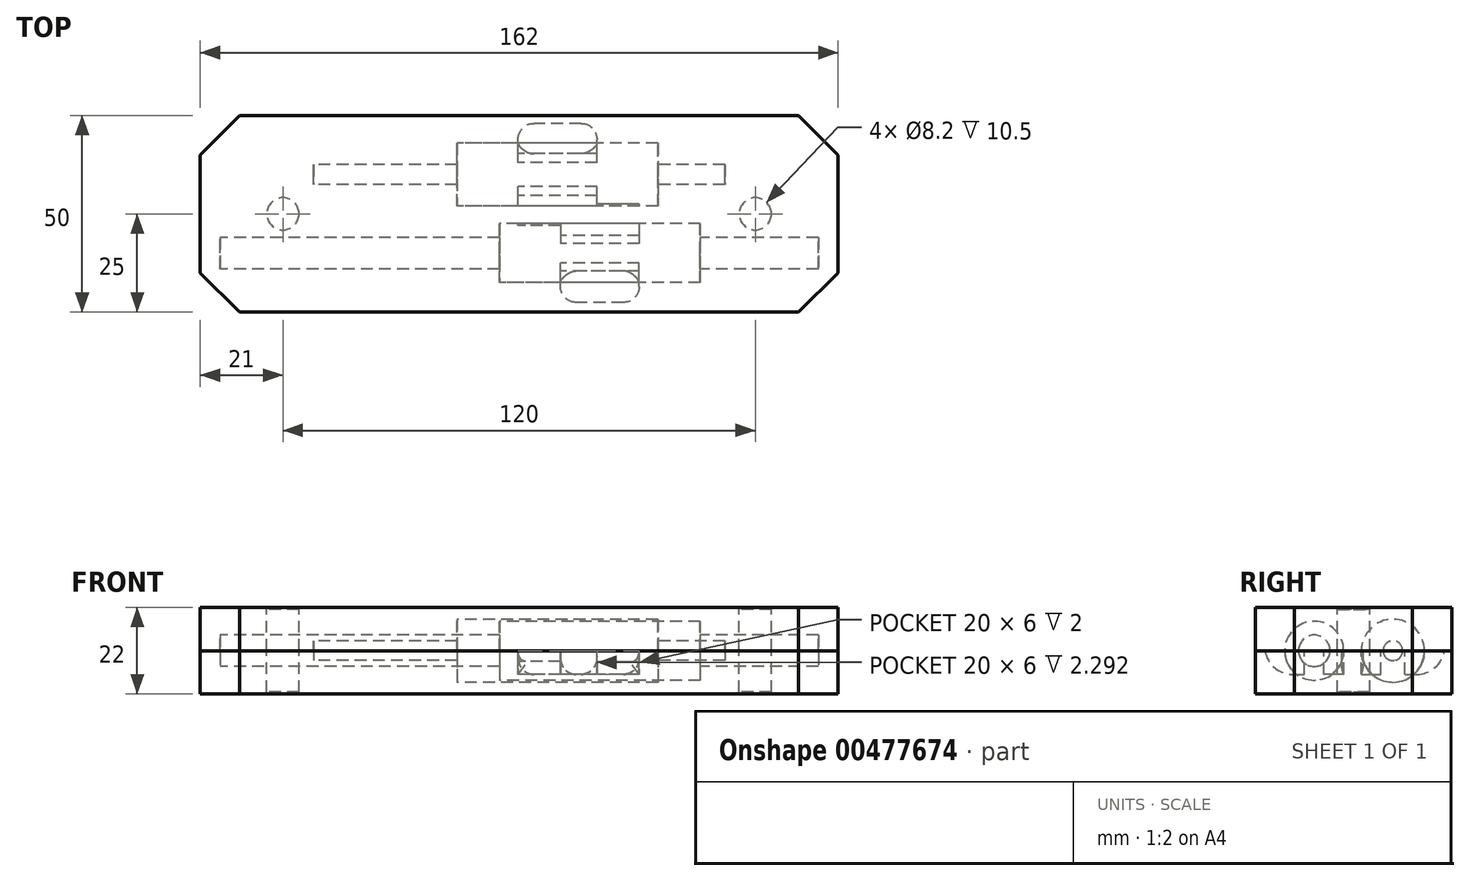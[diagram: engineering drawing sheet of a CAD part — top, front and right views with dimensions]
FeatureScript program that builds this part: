
annotation { "Feature Type Name" : "Feature", "Feature Type Description" : "" }
export const myFeature = defineFeature(function(context is Context, id is Id, definition is map)
    precondition{}
    {
        {
            var Q0;
            Q0=qCreatedBy(makeId("Top.planeOp"),FACE);
            var sketch = newSketch(context, id + "F0", { "sketchPlane" : qUnion([Q0])});
            skLineSegment(sketch, "E0", {"start": v(-52.25, 10) * mm, "end": v(52.25, 10) * mm});
            skLineSegment(sketch, "E1", {"start": v(52.25, 10) * mm, "end": v(52.25, 12.5) * mm});
            skLineSegment(sketch, "E2", {"start": v(52.25, 12.5) * mm, "end": v(35.25, 12.5) * mm});
            skLineSegment(sketch, "E3", {"start": v(35.25, 12.5) * mm, "end": v(35.25, 18) * mm});
            skLineSegment(sketch, "E4", {"start": v(35.25, 18) * mm, "end": v(-15.75, 18) * mm});
            skLineSegment(sketch, "E5", {"start": v(-15.75, 18) * mm, "end": v(-15.75, 12.5) * mm});
            skLineSegment(sketch, "E6", {"start": v(-15.75, 12.5) * mm, "end": v(-52.25, 12.5) * mm});
            skLineSegment(sketch, "E7", {"start": v(-52.25, 12.5) * mm, "end": v(-52.25, 10) * mm});
            skLineSegment(sketch, "E8", {"start": v(-76, -10) * mm, "end": v(76, -10) * mm});
            skLineSegment(sketch, "E9", {"start": v(76, -10) * mm, "end": v(76, -14) * mm});
            skLineSegment(sketch, "E10", {"start": v(76, -14) * mm, "end": v(46, -14) * mm});
            skLineSegment(sketch, "E11", {"start": v(46, -14) * mm, "end": v(46, -17.5) * mm});
            skLineSegment(sketch, "E12", {"start": v(46, -17.5) * mm, "end": v(-5, -17.5) * mm});
            skLineSegment(sketch, "E13", {"start": v(-5, -17.5) * mm, "end": v(-5, -14) * mm});
            skLineSegment(sketch, "E14", {"start": v(-5, -14) * mm, "end": v(-76, -14) * mm});
            skLineSegment(sketch, "E15", {"start": v(-76, -14) * mm, "end": v(-76, -10) * mm});
            skLineSegment(sketch, "E16", {"start": v(0, -10) * mm, "end": v(0, 0) * mm, "construction": true});
            skLineSegment(sketch, "E17", {"start": v(0, 10) * mm, "end": v(0, 0) * mm, "construction": true});
            skSolve(sketch);
        }
        {
            var Q0;
            Q0=makeQuery(id+"F0.imprint","IMPRINT",FACE,{"disambiguationData":[TD([[makeQuery(id+"F0.imprint","IMPRINT",EDGE,{"derivedFrom":sQuery(id+"F0.wireOp",EDGE,"E0")}),1.0]])]});
            var Q1;
            Q1=sQuery(id+"F0.wireOp",EDGE,"E0");
            revolve(context, id + "F1", {"entities" : qUnion([Q0]), "axis" : qUnion([Q1]), "revolveType" : RevolveType.FULL});
        }
        {
            var Q0;
            Q0=makeQuery(id+"F0.imprint","IMPRINT",FACE,{"disambiguationData":[TD([[makeQuery(id+"F0.imprint","IMPRINT",EDGE,{"derivedFrom":sQuery(id+"F0.wireOp",EDGE,"E8")}),-1.0]])]});
            var Q1;
            Q1=sQuery(id+"F0.wireOp",EDGE,"E8");
            revolve(context, id + "F2", {"entities" : qUnion([Q0]), "axis" : qUnion([Q1]), "revolveType" : RevolveType.FULL});
        }
        {
            var Q0;
            Q0=qCreatedBy(makeId("Top.planeOp"),FACE);
            var sketch = newSketch(context, id + "F3", { "sketchPlane" : qUnion([Q0])});
            skLineSegment(sketch, "E18.bottom", {"start": v(81, -25) * mm, "end": v(-81, -25) * mm});
            skLineSegment(sketch, "E18.top", {"start": v(81, 25) * mm, "end": v(-81, 25) * mm});
            skLineSegment(sketch, "E18.left", {"start": v(81, -25) * mm, "end": v(81, 25) * mm});
            skLineSegment(sketch, "E18.right", {"start": v(-81, -25) * mm, "end": v(-81, 25) * mm});
            skPoint(sketch, "E18.middle", {"position": v(0, 0) * mm});
            skSolve(sketch);
        }
        {
            var Q0;
            Q0=makeQuery(id+"F3.imprint","IMPRINT",FACE,{"disambiguationData":[TD([[makeQuery(id+"F3.imprint","IMPRINT",EDGE,{"derivedFrom":sQuery(id+"F3.wireOp",EDGE,"E18.bottom")}),-1.0]])]});
            extrude(context, id + "F4", {"entities" : qUnion([Q0]), "oppositeDirection" : true, "depth" : 11 * mm});
        }
        {
            var Q0;
            Q0=makeQuery(id+"F4.opExtrude","CAP_FACE",FACE,{"disambiguationData":[OSD([sQuery(id+"F3.wireOp",EDGE,"E18.bottom"),sQuery(id+"F3.wireOp",EDGE,"E18.top"),sQuery(id+"F3.wireOp",EDGE,"E18.left"),sQuery(id+"F3.wireOp",EDGE,"E18.right")])],"isStart":true});
            var sketch = newSketch(context, id + "F5", { "sketchPlane" : qUnion([Q0])});
            skLineSegment(sketch, "E19.bottom", {"start": v(81, -25) * mm, "end": v(-81, -25) * mm});
            skLineSegment(sketch, "E19.top", {"start": v(81, 25) * mm, "end": v(-81, 25) * mm});
            skLineSegment(sketch, "E19.left", {"start": v(81, -25) * mm, "end": v(81, 25) * mm});
            skLineSegment(sketch, "E19.right", {"start": v(-81, -25) * mm, "end": v(-81, 25) * mm});
            skPoint(sketch, "E19.middle", {"position": v(0, 0) * mm});
            skSolve(sketch);
        }
        {
            var Q0;
            Q0=makeQuery(id+"F5.imprint","IMPRINT",FACE,{"disambiguationData":[TD([[makeQuery(id+"F5.imprint","IMPRINT",EDGE,{"derivedFrom":sQuery(id+"F5.wireOp",EDGE,"E19.bottom")}),-1.0]])]});
            var Q1;
            Q1=makeQuery(id+"F5.imprint","IMPRINT",FACE,{"disambiguationData":[TD([[makeQuery(id+"F5.imprint","IMPRINT",EDGE,{"derivedFrom":makeQuery(id+"F4.opExtrude","CAP_EDGE",EDGE,{"disambiguationData":[OSD([sQuery(id+"F3.wireOp",EDGE,"E18.bottom")])],"isStart":true})}),-1.0]])]});
            extrude(context, id + "F6", {"entities" : qUnion([Q0, Q1]), "depth" : 11 * mm});
        }
        {
            var Q0;
            Q0=makeQuery(id+"F6.opExtrude","CAP_FACE",FACE,{"disambiguationData":[OSD([sQuery(id+"F5.wireOp",EDGE,"E19.bottom"),sQuery(id+"F5.wireOp",EDGE,"E19.top"),sQuery(id+"F5.wireOp",EDGE,"E19.left"),sQuery(id+"F5.wireOp",EDGE,"E19.right")])],"isStart":true});
            var sketch = newSketch(context, id + "F7", { "sketchPlane" : qUnion([Q0])});
            skLineSegment(sketch, "E20.bottom", {"start": v(-81, 25) * mm, "end": v(81, 25) * mm});
            skLineSegment(sketch, "E20.top", {"start": v(-81, -25) * mm, "end": v(81, -25) * mm});
            skLineSegment(sketch, "E20.left", {"start": v(-81, 25) * mm, "end": v(-81, -25) * mm});
            skLineSegment(sketch, "E20.right", {"start": v(81, 25) * mm, "end": v(81, -25) * mm});
            skLineSegment(sketch, "E21.0", {"start": v(-83, 27) * mm, "end": v(-83, -27) * mm});
            skLineSegment(sketch, "E21.1", {"start": v(-83, 27) * mm, "end": v(83, 27) * mm});
            skLineSegment(sketch, "E21.2", {"start": v(83, 27) * mm, "end": v(83, -27) * mm});
            skLineSegment(sketch, "E21.3", {"start": v(-83, -27) * mm, "end": v(83, -27) * mm});
            skSolve(sketch);
        }
        {
            var Q0;
            Q0=makeQuery(id+"F4.opExtrude","SWEPT_EDGE",EDGE,{"disambiguationData":[OSD([sQuery(id+"F3.wireOp",EDGE,"E18.bottom"),sQuery(id+"F3.wireOp",EDGE,"E18.right")])]});
            var Q1;
            Q1=makeQuery(id+"F4.opExtrude","SWEPT_EDGE",EDGE,{"disambiguationData":[OSD([sQuery(id+"F3.wireOp",EDGE,"E18.top"),sQuery(id+"F3.wireOp",EDGE,"E18.right")])]});
            var Q2;
            Q2=makeQuery(id+"F4.opExtrude","SWEPT_EDGE",EDGE,{"disambiguationData":[OSD([sQuery(id+"F3.wireOp",EDGE,"E18.bottom"),sQuery(id+"F3.wireOp",EDGE,"E18.left")])]});
            var Q3;
            Q3=makeQuery(id+"F4.opExtrude","SWEPT_EDGE",EDGE,{"disambiguationData":[OSD([sQuery(id+"F3.wireOp",EDGE,"E18.top"),sQuery(id+"F3.wireOp",EDGE,"E18.left")])]});
            chamfer(context, id + "F8", {"entities" : qUnion([Q0, Q1, Q2, Q3]), "width" : 10 * mm, "tangentPropagation" : true});
        }
        {
            var Q0;
            Q0=makeQuery(id+"FrTvgTOctuqtWCn_4.opExtrude","SWEPT_EDGE",EDGE,{"disambiguationData":[OSD([sQuery(id+"F7.wireOp",EDGE,"E21.0"),sQuery(id+"F7.wireOp",EDGE,"E21.1")])]});
            var Q1;
            Q1=makeQuery(id+"FrTvgTOctuqtWCn_4.opExtrude","SWEPT_EDGE",EDGE,{"disambiguationData":[OSD([sQuery(id+"F7.wireOp",EDGE,"E21.1"),sQuery(id+"F7.wireOp",EDGE,"E21.2")])]});
            var Q2;
            Q2=makeQuery(id+"FrTvgTOctuqtWCn_4.boolean.opBoolean","MERGE",EDGE,{"derivedFrom":[makeQuery(id+"F6.opExtrude","SWEPT_EDGE",EDGE,{"disambiguationData":[OSD([sQuery(id+"F5.wireOp",EDGE,"E19.top"),sQuery(id+"F5.wireOp",EDGE,"E19.left")])]}),makeQuery(id+"FrTvgTOctuqtWCn_4.opExtrude","SWEPT_EDGE",EDGE,{"disambiguationData":[OSD([sQuery(id+"F7.wireOp",EDGE,"E20.top"),sQuery(id+"F7.wireOp",EDGE,"E20.right")])]})]});
            var Q3;
            Q3=makeQuery(id+"FrTvgTOctuqtWCn_4.boolean.opBoolean","MERGE",EDGE,{"derivedFrom":[makeQuery(id+"F6.opExtrude","SWEPT_EDGE",EDGE,{"disambiguationData":[OSD([sQuery(id+"F5.wireOp",EDGE,"E19.top"),sQuery(id+"F5.wireOp",EDGE,"E19.right")])]}),makeQuery(id+"FrTvgTOctuqtWCn_4.opExtrude","SWEPT_EDGE",EDGE,{"disambiguationData":[OSD([sQuery(id+"F7.wireOp",EDGE,"E20.top"),sQuery(id+"F7.wireOp",EDGE,"E20.left")])]})]});
            var Q4;
            Q4=makeQuery(id+"FrTvgTOctuqtWCn_4.boolean.opBoolean","MERGE",EDGE,{"derivedFrom":[makeQuery(id+"F6.opExtrude","SWEPT_EDGE",EDGE,{"disambiguationData":[OSD([sQuery(id+"F5.wireOp",EDGE,"E19.bottom"),sQuery(id+"F5.wireOp",EDGE,"E19.right")])]}),makeQuery(id+"FrTvgTOctuqtWCn_4.opExtrude","SWEPT_EDGE",EDGE,{"disambiguationData":[OSD([sQuery(id+"F7.wireOp",EDGE,"E20.bottom"),sQuery(id+"F7.wireOp",EDGE,"E20.left")])]})]});
            var Q5;
            Q5=makeQuery(id+"FrTvgTOctuqtWCn_4.boolean.opBoolean","MERGE",EDGE,{"derivedFrom":[makeQuery(id+"F6.opExtrude","SWEPT_EDGE",EDGE,{"disambiguationData":[OSD([sQuery(id+"F5.wireOp",EDGE,"E19.bottom"),sQuery(id+"F5.wireOp",EDGE,"E19.left")])]}),makeQuery(id+"FrTvgTOctuqtWCn_4.opExtrude","SWEPT_EDGE",EDGE,{"disambiguationData":[OSD([sQuery(id+"F7.wireOp",EDGE,"E20.bottom"),sQuery(id+"F7.wireOp",EDGE,"E20.right")])]})]});
            var Q6;
            Q6=makeQuery(id+"FrTvgTOctuqtWCn_4.opExtrude","SWEPT_EDGE",EDGE,{"disambiguationData":[OSD([sQuery(id+"F7.wireOp",EDGE,"E21.0"),sQuery(id+"F7.wireOp",EDGE,"E21.3")])]});
            var Q7;
            Q7=makeQuery(id+"FrTvgTOctuqtWCn_4.opExtrude","SWEPT_EDGE",EDGE,{"disambiguationData":[OSD([sQuery(id+"F7.wireOp",EDGE,"E21.2"),sQuery(id+"F7.wireOp",EDGE,"E21.3")])]});
            chamfer(context, id + "F9", {"entities" : qUnion([Q0, Q1, Q2, Q3, Q4, Q5, Q6, Q7]), "width" : 10 * mm, "tangentPropagation" : true});
        }
        {
            var Q0;
            Q0=makeQuery(id+"F4.opExtrude","CAP_FACE",FACE,{"disambiguationData":[OSD([sQuery(id+"F3.wireOp",EDGE,"E18.bottom"),sQuery(id+"F3.wireOp",EDGE,"E18.top"),sQuery(id+"F3.wireOp",EDGE,"E18.left"),sQuery(id+"F3.wireOp",EDGE,"E18.right")])],"isStart":true});
            var sketch = newSketch(context, id + "F10", { "sketchPlane" : qUnion([Q0])});
            skText(sketch, "E22", { "text": "Sensor", "fontName": "OpenSans-Regular.ttf"});
            skText(sketch, "E23", { "text": "Heater", "fontName": "OpenSans-Regular.ttf"});
            skLineSegment(sketch, "E24", {"start": v(0, 35.83) * mm, "end": v(0, 0) * mm});
            skLineSegment(sketch, "E25", {"start": v(0, -33.77) * mm, "end": v(0, 0) * mm});
            const initialGuessF10  = {"E22": [-0.01813, 0.03583, 1, 0, 0.008], "E23": [-0.01793, -0.04177, 1, 0, 0.008]};
            skSetInitialGuess(sketch, initialGuessF10);
            skSolve(sketch);
        }
        {
            var Q0;
            {var subQ0=sQuery(id+"F3.wireOp",EDGE,"E18.right");var subQ1=sQuery(id+"F3.wireOp",EDGE,"E18.left");var subQ2=sQuery(id+"F3.wireOp",EDGE,"E18.top");var subQ3=sQuery(id+"F3.wireOp",EDGE,"E18.bottom");Q0=makeQuery(id+"FiV2CEHEbZasTx0_4.boolean.opBoolean","SPLIT",FACE,{"disambiguationData":[TD([makeQuery(id+"F4.opExtrude","SWEPT_FACE",FACE,{"disambiguationData":[OSD([subQ3])]})])],"derivedFrom":makeQuery(id+"F4.opExtrude","CAP_FACE",FACE,{"disambiguationData":[OSD([subQ3,subQ2,subQ1,subQ0])],"isStart":true})});}
            var sketch = newSketch(context, id + "F11", { "sketchPlane" : qUnion([Q0])});
            skPoint(sketch, "E26.middle", {"position": v(0, 0) * mm});
            skLineSegment(sketch, "E27", {"start": v(-60, 0) * mm, "end": v(60, 0) * mm, "construction": true});
            skCircle(sketch, "E28", {"center": v(-60, 0) * mm, "radius": 4.1 * mm});
            skCircle(sketch, "E29", {"center": v(60, 0) * mm, "radius": 4.1 * mm});
            skSolve(sketch);
        }
        {
            var Q0;
            Q0=makeQuery(id+"F11.imprint","IMPRINT",FACE,{"disambiguationData":[TD([[makeQuery(id+"F11.imprint","IMPRINT",EDGE,{"derivedFrom":sQuery(id+"F11.wireOp",EDGE,"E28")}),1.0]])]});
            var Q1;
            Q1=makeQuery(id+"F11.imprint","IMPRINT",FACE,{"disambiguationData":[TD([[makeQuery(id+"F11.imprint","IMPRINT",EDGE,{"derivedFrom":sQuery(id+"F11.wireOp",EDGE,"E29")}),1.0]])]});
            extrude(context, id + "F12", {"entities" : qUnion([Q0, Q1]), "operationType" : NewBodyOperationType.REMOVE, "endBound" : BoundingType.SYMMETRIC, "oppositeDirection" : true, "depth" : 21 * mm});
        }
        {
            var Q0;
            Q0=makeQuery(id+"F1.opRevolve","SWEPT_BODY",BODY,{"disambiguationData":[OSD([sQuery(id+"F0.wireOp",EDGE,"E0"),sQuery(id+"F0.wireOp",EDGE,"E1"),sQuery(id+"F0.wireOp",EDGE,"E2"),sQuery(id+"F0.wireOp",EDGE,"E3"),sQuery(id+"F0.wireOp",EDGE,"E4"),sQuery(id+"F0.wireOp",EDGE,"E5"),sQuery(id+"F0.wireOp",EDGE,"E6"),sQuery(id+"F0.wireOp",EDGE,"E7")])]});
            var Q1;
            Q1=makeQuery(id+"F2.opRevolve","SWEPT_BODY",BODY,{"disambiguationData":[OSD([sQuery(id+"F0.wireOp",EDGE,"E8"),sQuery(id+"F0.wireOp",EDGE,"E9"),sQuery(id+"F0.wireOp",EDGE,"E10"),sQuery(id+"F0.wireOp",EDGE,"E11"),sQuery(id+"F0.wireOp",EDGE,"E12"),sQuery(id+"F0.wireOp",EDGE,"E13"),sQuery(id+"F0.wireOp",EDGE,"E14"),sQuery(id+"F0.wireOp",EDGE,"E15")])]});
            var Q2;
            Q2=makeQuery(id+"F4.opExtrude","SWEPT_BODY",BODY,{"disambiguationData":[OSD([sQuery(id+"F3.wireOp",EDGE,"E18.bottom"),sQuery(id+"F3.wireOp",EDGE,"E18.top"),sQuery(id+"F3.wireOp",EDGE,"E18.left"),sQuery(id+"F3.wireOp",EDGE,"E18.right")])]});
            booleanBodies(context, id + "F13", {"operationType" : BooleanOperationType.SUBTRACTION, "tools" : qUnion([Q0, Q1]), "targets" : qUnion([Q2]), "keepTools" : true});
        }
        {
            var Q0;
            Q0=makeQuery(id+"F2.opRevolve","SWEPT_BODY",BODY,{"disambiguationData":[OSD([sQuery(id+"F0.wireOp",EDGE,"E8"),sQuery(id+"F0.wireOp",EDGE,"E9"),sQuery(id+"F0.wireOp",EDGE,"E10"),sQuery(id+"F0.wireOp",EDGE,"E11"),sQuery(id+"F0.wireOp",EDGE,"E12"),sQuery(id+"F0.wireOp",EDGE,"E13"),sQuery(id+"F0.wireOp",EDGE,"E14"),sQuery(id+"F0.wireOp",EDGE,"E15")])]});
            var Q1;
            Q1=makeQuery(id+"F1.opRevolve","SWEPT_BODY",BODY,{"disambiguationData":[OSD([sQuery(id+"F0.wireOp",EDGE,"E0"),sQuery(id+"F0.wireOp",EDGE,"E1"),sQuery(id+"F0.wireOp",EDGE,"E2"),sQuery(id+"F0.wireOp",EDGE,"E3"),sQuery(id+"F0.wireOp",EDGE,"E4"),sQuery(id+"F0.wireOp",EDGE,"E5"),sQuery(id+"F0.wireOp",EDGE,"E6"),sQuery(id+"F0.wireOp",EDGE,"E7")])]});
            var Q2;
            Q2=makeQuery(id+"F6.opExtrude","SWEPT_BODY",BODY,{"disambiguationData":[OSD([sQuery(id+"F5.wireOp",EDGE,"E19.bottom"),sQuery(id+"F5.wireOp",EDGE,"E19.top"),sQuery(id+"F5.wireOp",EDGE,"E19.left"),sQuery(id+"F5.wireOp",EDGE,"E19.right")])]});
            booleanBodies(context, id + "F14", {"operationType" : BooleanOperationType.SUBTRACTION, "tools" : qUnion([Q0, Q1]), "targets" : qUnion([Q2]), "keepTools" : true});
        }
        {
            var Q0;
            Q0=makeQuery(id+"F6.opExtrude","CAP_FACE",FACE,{"disambiguationData":[OSD([sQuery(id+"F5.wireOp",EDGE,"E19.bottom"),sQuery(id+"F5.wireOp",EDGE,"E19.top"),sQuery(id+"F5.wireOp",EDGE,"E19.left"),sQuery(id+"F5.wireOp",EDGE,"E19.right")])],"isStart":false});
            var sketch = newSketch(context, id + "F15", { "sketchPlane" : qUnion([Q0])});
            skText(sketch, "E30", { "text": "Heater \n", "fontName": "OpenSans-Regular.ttf"});
            skText(sketch, "E31", { "text": "Block\n", "fontName": "OpenSans-Regular.ttf"});
            skLineSegment(sketch, "E32", {"start": v(0, -5) * mm, "end": v(0, 5) * mm});
            const initialGuessF15  = {"E30": [-0.06725, 0.005, 1, 0, 0.03], "E31": [-0.05334, -0.035, 1, 0, 0.03]};
            skSetInitialGuess(sketch, initialGuessF15);
            skSolve(sketch);
        }
        {
            var Q0;
            {var subQ0=sQuery(id+"F3.wireOp",EDGE,"E18.right");var subQ1=sQuery(id+"F3.wireOp",EDGE,"E18.left");var subQ2=sQuery(id+"F3.wireOp",EDGE,"E18.top");var subQ3=sQuery(id+"F3.wireOp",EDGE,"E18.bottom");Q0=makeQuery(id+"FiV2CEHEbZasTx0_4.boolean.opBoolean","SPLIT",FACE,{"disambiguationData":[TD([makeQuery(id+"F4.opExtrude","SWEPT_FACE",FACE,{"disambiguationData":[OSD([subQ3])]})])],"derivedFrom":makeQuery(id+"F4.opExtrude","CAP_FACE",FACE,{"disambiguationData":[OSD([subQ3,subQ2,subQ1,subQ0])],"isStart":true})});}
            var sketch = newSketch(context, id + "F16", { "sketchPlane" : qUnion([Q0])});
            skLineSegment(sketch, "E33.bottom", {"start": v(19.75, 13) * mm, "end": v(-0.25, 13) * mm});
            skLineSegment(sketch, "E33.top", {"start": v(19.75, 23) * mm, "end": v(-0.25, 23) * mm});
            skLineSegment(sketch, "E33.left", {"start": v(19.75, 13) * mm, "end": v(19.75, 23) * mm});
            skLineSegment(sketch, "E33.right", {"start": v(-0.25, 13) * mm, "end": v(-0.25, 23) * mm});
            skPoint(sketch, "E33.middle", {"position": v(9.75, 18) * mm});
            skLineSegment(sketch, "E34.bottom", {"start": v(19.75, -3) * mm, "end": v(-0.25, -3) * mm});
            skLineSegment(sketch, "E34.top", {"start": v(19.75, 7) * mm, "end": v(-0.25, 7) * mm});
            skLineSegment(sketch, "E34.left", {"start": v(19.75, -3) * mm, "end": v(19.75, 7) * mm});
            skLineSegment(sketch, "E34.right", {"start": v(-0.25, -3) * mm, "end": v(-0.25, 7) * mm});
            skPoint(sketch, "E34.middle", {"position": v(9.75, 2) * mm});
            skLineSegment(sketch, "E35.bottom", {"start": v(30.5, 2.5) * mm, "end": v(10.5, 2.5) * mm});
            skLineSegment(sketch, "E35.top", {"start": v(30.5, -7.5) * mm, "end": v(10.5, -7.5) * mm});
            skLineSegment(sketch, "E35.left", {"start": v(30.5, 2.5) * mm, "end": v(30.5, -7.5) * mm});
            skLineSegment(sketch, "E35.right", {"start": v(10.5, 2.5) * mm, "end": v(10.5, -7.5) * mm});
            skPoint(sketch, "E35.middle", {"position": v(20.5, -2.5) * mm});
            skLineSegment(sketch, "E36.bottom", {"start": v(30.5, -22.5) * mm, "end": v(10.5, -22.5) * mm});
            skLineSegment(sketch, "E36.top", {"start": v(30.5, -12.5) * mm, "end": v(10.5, -12.5) * mm});
            skLineSegment(sketch, "E36.left", {"start": v(30.5, -22.5) * mm, "end": v(30.5, -12.5) * mm});
            skLineSegment(sketch, "E36.right", {"start": v(10.5, -22.5) * mm, "end": v(10.5, -12.5) * mm});
            skPoint(sketch, "E36.middle", {"position": v(20.5, -17.5) * mm});
            skSolve(sketch);
        }
        {
            var Q0;
            {var subQ0=sQuery(id+"F16.wireOp",EDGE,"E33.top");Q0=makeQuery(id+"F16.imprint","IMPRINT",FACE,{"disambiguationData":[TD([[makeQuery(id+"F16.imprint","IMPRINT",EDGE,{"derivedFrom":subQ0}),1.0]])]});}
            var Q1;
            {var subQ0=sQuery(id+"F16.wireOp",EDGE,"E34.bottom");Q1=makeQuery(id+"F16.imprint","IMPRINT",FACE,{"disambiguationData":[TD([[makeQuery(id+"F16.imprint","IMPRINT",EDGE,{"derivedFrom":subQ0}),-1.0]])]});}
            var Q2;
            {var subQ0=sQuery(id+"F16.wireOp",EDGE,"E35.bottom");Q2=makeQuery(id+"F16.imprint","IMPRINT",FACE,{"disambiguationData":[TD([[makeQuery(id+"F16.imprint","IMPRINT",EDGE,{"derivedFrom":subQ0}),1.0]])]});}
            var Q3;
            {var subQ0=sQuery(id+"F16.wireOp",EDGE,"E34.top");Q3=makeQuery(id+"F16.imprint","IMPRINT",FACE,{"disambiguationData":[TD([[makeQuery(id+"F16.imprint","IMPRINT",EDGE,{"derivedFrom":subQ0}),1.0]])]});}
            var Q4;
            {var subQ0=sQuery(id+"F16.wireOp",EDGE,"E33.bottom");Q4=makeQuery(id+"F16.imprint","IMPRINT",FACE,{"disambiguationData":[TD([[makeQuery(id+"F16.imprint","IMPRINT",EDGE,{"derivedFrom":subQ0}),-1.0]])]});}
            var Q5;
            {var subQ0=sQuery(id+"F16.wireOp",EDGE,"E35.top");Q5=makeQuery(id+"F16.imprint","IMPRINT",FACE,{"disambiguationData":[TD([[makeQuery(id+"F16.imprint","IMPRINT",EDGE,{"derivedFrom":subQ0}),-1.0]])]});}
            var Q6;
            {var subQ0=sQuery(id+"F16.wireOp",EDGE,"E36.top");Q6=makeQuery(id+"F16.imprint","IMPRINT",FACE,{"disambiguationData":[TD([[makeQuery(id+"F16.imprint","IMPRINT",EDGE,{"derivedFrom":subQ0}),1.0]])]});}
            var Q7;
            {var subQ0=sQuery(id+"F16.wireOp",EDGE,"E36.bottom");Q7=makeQuery(id+"F16.imprint","IMPRINT",FACE,{"disambiguationData":[TD([[makeQuery(id+"F16.imprint","IMPRINT",EDGE,{"derivedFrom":subQ0}),-1.0]])]});}
            extrude(context, id + "F17", {"entities" : qUnion([Q0, Q1, Q2, Q3, Q4, Q5, Q6, Q7]), "operationType" : NewBodyOperationType.REMOVE, "oppositeDirection" : true, "depth" : 6 * mm});
        }
        {
            var Q0;
            Q0=makeQuery(id+"F17.boolean.opBoolean","COPY",EDGE,{"derivedFrom":makeQuery(id+"F17.opExtrude","CAP_EDGE",EDGE,{"disambiguationData":[OSD([sQuery(id+"F16.wireOp",EDGE,"E35.bottom")])],"isStart":false})});
            var Q1;
            Q1=makeQuery(id+"F17.boolean.opBoolean","COPY",EDGE,{"derivedFrom":makeQuery(id+"F17.opExtrude","CAP_EDGE",EDGE,{"disambiguationData":[OSD([sQuery(id+"F16.wireOp",EDGE,"E36.bottom")])],"isStart":false})});
            var Q2;
            Q2=makeQuery(id+"F17.boolean.opBoolean","COPY",EDGE,{"derivedFrom":makeQuery(id+"F17.opExtrude","CAP_EDGE",EDGE,{"disambiguationData":[OSD([sQuery(id+"F16.wireOp",EDGE,"E34.bottom")])],"isStart":false})});
            var Q3;
            Q3=makeQuery(id+"F17.boolean.opBoolean","COPY",EDGE,{"derivedFrom":makeQuery(id+"F17.opExtrude","CAP_EDGE",EDGE,{"disambiguationData":[OSD([sQuery(id+"F16.wireOp",EDGE,"E33.top")])],"isStart":false})});
            fillet(context, id + "F18", {"entities" : qUnion([Q0, Q1, Q2, Q3]), "radius" : 7 * mm, "tangentPropagation" : true, "allowEdgeOverflow" : false});
        }
        {
            var Q0;
            Q0=makeQuery(id+"F18.opFillet","BLEND_EDGE",EDGE,{"blendedFrom":[makeQuery(id+"F17.boolean.opBoolean","COPY",EDGE,{"derivedFrom":makeQuery(id+"F17.opExtrude","CAP_EDGE",EDGE,{"disambiguationData":[OSD([sQuery(id+"F16.wireOp",EDGE,"E36.bottom")])],"isStart":false})}),makeQuery(id+"F17.boolean.opBoolean","COPY",FACE,{"derivedFrom":makeQuery(id+"F17.opExtrude","SWEPT_FACE",FACE,{"disambiguationData":[OSD([sQuery(id+"F16.wireOp",EDGE,"E36.right")])]})})],"blendedInto":[makeQuery(id+"F17.boolean.opBoolean","COPY",FACE,{"derivedFrom":makeQuery(id+"F17.opExtrude","SWEPT_FACE",FACE,{"disambiguationData":[OSD([sQuery(id+"F16.wireOp",EDGE,"E36.right")])]})})]});
            var Q1;
            Q1=makeQuery(id+"F18.opFillet","BLEND_EDGE",EDGE,{"blendedFrom":[makeQuery(id+"F17.boolean.opBoolean","COPY",EDGE,{"derivedFrom":makeQuery(id+"F17.opExtrude","CAP_EDGE",EDGE,{"disambiguationData":[OSD([sQuery(id+"F16.wireOp",EDGE,"E36.bottom")])],"isStart":false})}),makeQuery(id+"F17.boolean.opBoolean","COPY",FACE,{"derivedFrom":makeQuery(id+"F17.opExtrude","SWEPT_FACE",FACE,{"disambiguationData":[OSD([sQuery(id+"F16.wireOp",EDGE,"E36.left")])]})})],"blendedInto":[makeQuery(id+"F17.boolean.opBoolean","COPY",FACE,{"derivedFrom":makeQuery(id+"F17.opExtrude","SWEPT_FACE",FACE,{"disambiguationData":[OSD([sQuery(id+"F16.wireOp",EDGE,"E36.left")])]})})]});
            var Q2;
            Q2=makeQuery(id+"F18.opFillet","BLEND_EDGE",EDGE,{"blendedFrom":[makeQuery(id+"F17.boolean.opBoolean","COPY",EDGE,{"derivedFrom":makeQuery(id+"F17.opExtrude","CAP_EDGE",EDGE,{"disambiguationData":[OSD([sQuery(id+"F16.wireOp",EDGE,"E35.bottom")])],"isStart":false})}),makeQuery(id+"F17.boolean.opBoolean","COPY",FACE,{"derivedFrom":makeQuery(id+"F17.opExtrude","SWEPT_FACE",FACE,{"disambiguationData":[OSD([sQuery(id+"F16.wireOp",EDGE,"E35.right")])]})})],"blendedInto":[makeQuery(id+"F17.boolean.opBoolean","COPY",FACE,{"derivedFrom":makeQuery(id+"F17.opExtrude","SWEPT_FACE",FACE,{"disambiguationData":[OSD([sQuery(id+"F16.wireOp",EDGE,"E35.right")])]})})]});
            var Q3;
            Q3=makeQuery(id+"F18.opFillet","BLEND_EDGE",EDGE,{"blendedFrom":[makeQuery(id+"F17.boolean.opBoolean","COPY",EDGE,{"derivedFrom":makeQuery(id+"F17.opExtrude","CAP_EDGE",EDGE,{"disambiguationData":[OSD([sQuery(id+"F16.wireOp",EDGE,"E35.bottom")])],"isStart":false})}),makeQuery(id+"F17.boolean.opBoolean","COPY",FACE,{"derivedFrom":makeQuery(id+"F17.opExtrude","SWEPT_FACE",FACE,{"disambiguationData":[OSD([sQuery(id+"F16.wireOp",EDGE,"E35.left")])]})})],"blendedInto":[makeQuery(id+"F17.boolean.opBoolean","COPY",FACE,{"derivedFrom":makeQuery(id+"F17.opExtrude","SWEPT_FACE",FACE,{"disambiguationData":[OSD([sQuery(id+"F16.wireOp",EDGE,"E35.left")])]})})]});
            var Q4;
            Q4=makeQuery(id+"F18.opFillet","BLEND_EDGE",EDGE,{"blendedFrom":[makeQuery(id+"F17.boolean.opBoolean","COPY",EDGE,{"derivedFrom":makeQuery(id+"F17.opExtrude","CAP_EDGE",EDGE,{"disambiguationData":[OSD([sQuery(id+"F16.wireOp",EDGE,"E33.top")])],"isStart":false})}),makeQuery(id+"F17.boolean.opBoolean","COPY",FACE,{"derivedFrom":makeQuery(id+"F17.opExtrude","SWEPT_FACE",FACE,{"disambiguationData":[OSD([sQuery(id+"F16.wireOp",EDGE,"E33.left")])]})})],"blendedInto":[makeQuery(id+"F17.boolean.opBoolean","COPY",FACE,{"derivedFrom":makeQuery(id+"F17.opExtrude","SWEPT_FACE",FACE,{"disambiguationData":[OSD([sQuery(id+"F16.wireOp",EDGE,"E33.left")])]})})]});
            var Q5;
            Q5=makeQuery(id+"F18.opFillet","BLEND_EDGE",EDGE,{"blendedFrom":[makeQuery(id+"F17.boolean.opBoolean","COPY",EDGE,{"derivedFrom":makeQuery(id+"F17.opExtrude","CAP_EDGE",EDGE,{"disambiguationData":[OSD([sQuery(id+"F16.wireOp",EDGE,"E33.top")])],"isStart":false})}),makeQuery(id+"F17.boolean.opBoolean","COPY",FACE,{"derivedFrom":makeQuery(id+"F17.opExtrude","SWEPT_FACE",FACE,{"disambiguationData":[OSD([sQuery(id+"F16.wireOp",EDGE,"E33.right")])]})})],"blendedInto":[makeQuery(id+"F17.boolean.opBoolean","COPY",FACE,{"derivedFrom":makeQuery(id+"F17.opExtrude","SWEPT_FACE",FACE,{"disambiguationData":[OSD([sQuery(id+"F16.wireOp",EDGE,"E33.right")])]})})]});
            var Q6;
            Q6=makeQuery(id+"F18.opFillet","BLEND_EDGE",EDGE,{"blendedFrom":[makeQuery(id+"F17.boolean.opBoolean","COPY",EDGE,{"derivedFrom":makeQuery(id+"F17.opExtrude","CAP_EDGE",EDGE,{"disambiguationData":[OSD([sQuery(id+"F16.wireOp",EDGE,"E34.bottom")])],"isStart":false})}),makeQuery(id+"F17.boolean.opBoolean","COPY",FACE,{"derivedFrom":makeQuery(id+"F17.opExtrude","SWEPT_FACE",FACE,{"disambiguationData":[OSD([sQuery(id+"F16.wireOp",EDGE,"E34.right")])]})})],"blendedInto":[makeQuery(id+"F17.boolean.opBoolean","COPY",FACE,{"derivedFrom":makeQuery(id+"F17.opExtrude","SWEPT_FACE",FACE,{"disambiguationData":[OSD([sQuery(id+"F16.wireOp",EDGE,"E34.right")])]})})]});
            var Q7;
            Q7=makeQuery(id+"F18.opFillet","BLEND_EDGE",EDGE,{"blendedFrom":[makeQuery(id+"F17.boolean.opBoolean","COPY",EDGE,{"derivedFrom":makeQuery(id+"F17.opExtrude","CAP_EDGE",EDGE,{"disambiguationData":[OSD([sQuery(id+"F16.wireOp",EDGE,"E34.bottom")])],"isStart":false})}),makeQuery(id+"F17.boolean.opBoolean","COPY",FACE,{"derivedFrom":makeQuery(id+"F17.opExtrude","SWEPT_FACE",FACE,{"disambiguationData":[OSD([sQuery(id+"F16.wireOp",EDGE,"E34.left")])]})})],"blendedInto":[makeQuery(id+"F17.boolean.opBoolean","COPY",FACE,{"derivedFrom":makeQuery(id+"F17.opExtrude","SWEPT_FACE",FACE,{"disambiguationData":[OSD([sQuery(id+"F16.wireOp",EDGE,"E34.left")])]})})]});
            fillet(context, id + "F19", {"entities" : qUnion([Q0, Q1, Q2, Q3, Q4, Q5, Q6, Q7]), "radius" : 4 * mm, "tangentPropagation" : true, "allowEdgeOverflow" : false});
        }
    });
